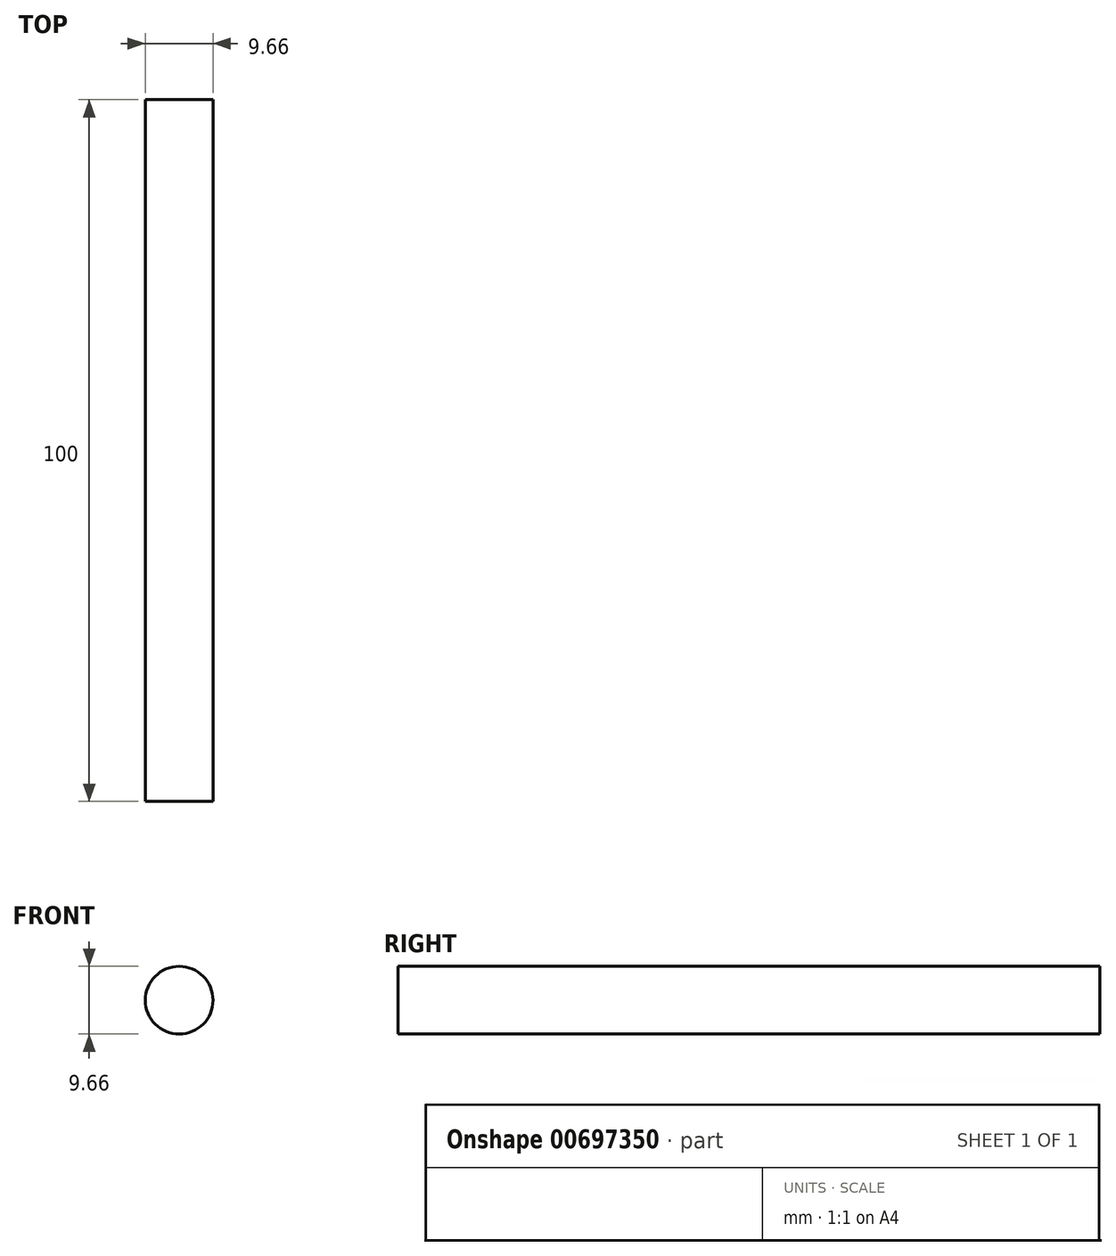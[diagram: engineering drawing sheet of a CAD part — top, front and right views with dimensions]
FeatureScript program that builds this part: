
annotation { "Feature Type Name" : "Feature", "Feature Type Description" : "" }
export const myFeature = defineFeature(function(context is Context, id is Id, definition is map)
    precondition{}
    {
        {
            var Q0;
            Q0=qCreatedBy(makeId("Front.planeOp"),FACE);
            var sketch = newSketch(context, id + "F0", { "sketchPlane" : qUnion([Q0])});
            skCircle(sketch, "E0", {"center": v(0, 0) * mm, "radius": 4.83 * mm});
            skSolve(sketch);
        }
        {
            var Q0;
            Q0 = qSketchRegion(id + "F0", true);
            extrude(context, id + "F1", {"entities" : qUnion([Q0]), "depth" : 100 * mm, "offsetDistance" : 25 * mm});
        }
    });
